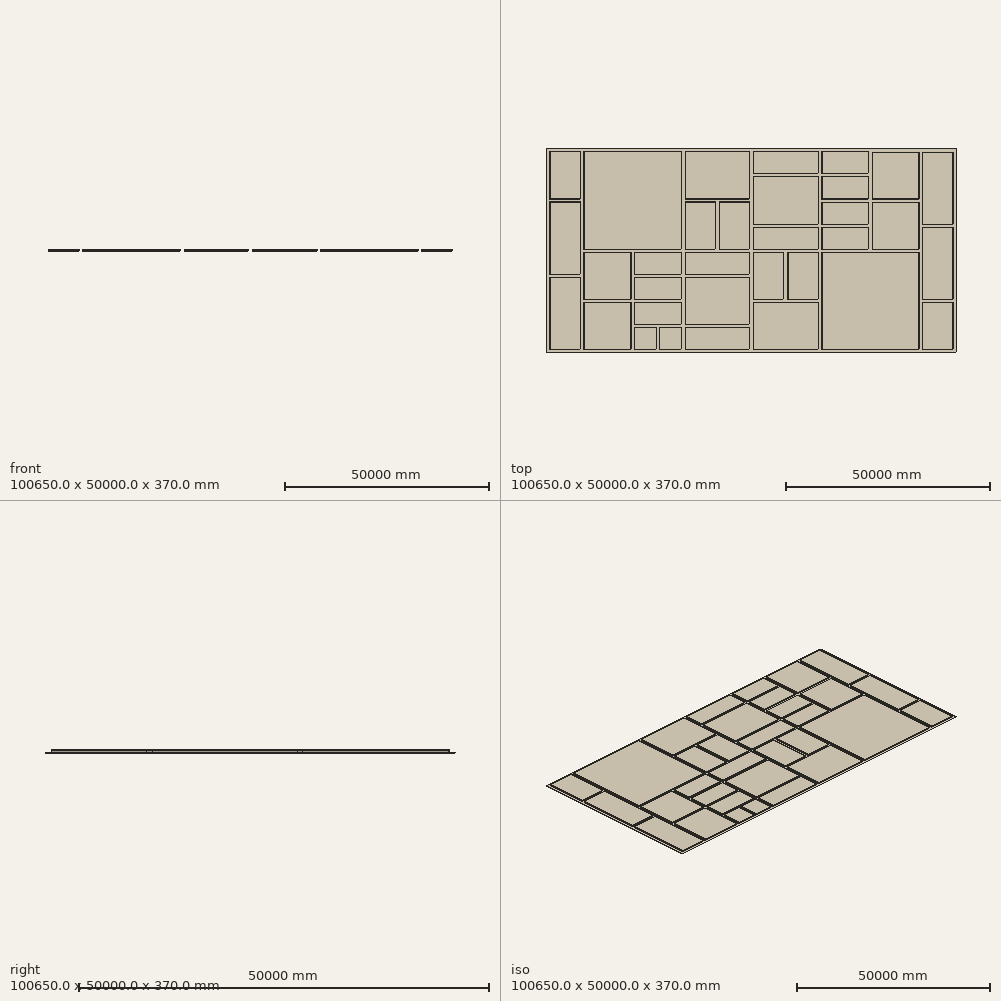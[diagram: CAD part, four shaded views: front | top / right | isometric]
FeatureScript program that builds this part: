
annotation { "Feature Type Name" : "Feature", "Feature Type Description" : "" }
export const myFeature = defineFeature(function(context is Context, id is Id, definition is map)
    precondition{}
    {
        {
            var Q0;
            Q0=qCreatedBy(makeId("Top.planeOp"),FACE);
            var sketch = newSketch(context, id + "F0", { "sketchPlane" : qUnion([Q0])});
            skLineSegment(sketch, "E0.bottom", {"start": v(50325, 25000) * mm, "end": v(-50325, 25000) * mm});
            skLineSegment(sketch, "E0.top", {"start": v(50325, -25000) * mm, "end": v(-50325, -25000) * mm});
            skLineSegment(sketch, "E0.left", {"start": v(50325, 25000) * mm, "end": v(50325, -25000) * mm});
            skLineSegment(sketch, "E0.right", {"start": v(-50325, 25000) * mm, "end": v(-50325, -25000) * mm});
            skPoint(sketch, "E0.middle", {"position": v(0, 0) * mm});
            skLineSegment(sketch, "E1", {"start": v(-50325, 0) * mm, "end": v(50325, 0) * mm, "construction": true});
            skLineSegment(sketch, "E2", {"start": v(-50688.62, 0) * mm, "end": v(50688.62, 0) * mm, "construction": true});
            skLineSegment(sketch, "E3.bottom", {"start": v(-16275, 11925) * mm, "end": v(-8775, 11925) * mm});
            skLineSegment(sketch, "E3.top", {"start": v(-16275, 283.33) * mm, "end": v(-8775, 283.33) * mm});
            skLineSegment(sketch, "E3.left", {"start": v(-16275, 11925) * mm, "end": v(-16275, 283.33) * mm});
            skLineSegment(sketch, "E3.right", {"start": v(-8775, 11925) * mm, "end": v(-8775, 283.33) * mm});
            skLineSegment(sketch, "E4.bottom", {"start": v(425, 18104.17) * mm, "end": v(16425, 18104.17) * mm});
            skLineSegment(sketch, "E4.top", {"start": v(425, 6391.67) * mm, "end": v(16425, 6391.67) * mm});
            skLineSegment(sketch, "E4.left", {"start": v(425, 18104.17) * mm, "end": v(425, 6391.67) * mm});
            skLineSegment(sketch, "E4.right", {"start": v(16425, 18104.17) * mm, "end": v(16425, 6391.67) * mm});
            skLineSegment(sketch, "E5.bottom", {"start": v(29625, 24141.67) * mm, "end": v(41125, 24141.67) * mm});
            skLineSegment(sketch, "E5.top", {"start": v(29625, 12641.67) * mm, "end": v(41125, 12641.67) * mm});
            skLineSegment(sketch, "E5.left", {"start": v(29625, 24141.67) * mm, "end": v(29625, 12641.67) * mm});
            skLineSegment(sketch, "E5.right", {"start": v(41125, 24141.67) * mm, "end": v(41125, 12641.67) * mm});
            skLineSegment(sketch, "E6.bottom", {"start": v(41975, 24141.67) * mm, "end": v(49475, 24141.67) * mm});
            skLineSegment(sketch, "E6.top", {"start": v(41975, 6391.67) * mm, "end": v(49475, 6391.67) * mm});
            skLineSegment(sketch, "E6.left", {"start": v(41975, 24141.67) * mm, "end": v(41975, 6391.67) * mm});
            skLineSegment(sketch, "E6.right", {"start": v(49475, 24141.67) * mm, "end": v(49475, 6391.67) * mm});
            skLineSegment(sketch, "E7.bottom", {"start": v(-49475, 24283.33) * mm, "end": v(-41975, 24283.33) * mm});
            skLineSegment(sketch, "E7.top", {"start": v(-49475, 12641.67) * mm, "end": v(-41975, 12641.67) * mm});
            skLineSegment(sketch, "E7.left", {"start": v(-49475, 24283.33) * mm, "end": v(-49475, 12641.67) * mm});
            skLineSegment(sketch, "E7.right", {"start": v(-41975, 24283.33) * mm, "end": v(-41975, 12641.67) * mm});
            skLineSegment(sketch, "E8.bottom", {"start": v(-49475, 11925) * mm, "end": v(-41975, 11925) * mm});
            skLineSegment(sketch, "E8.top", {"start": v(-49475, -5862.5) * mm, "end": v(-41975, -5862.5) * mm});
            skLineSegment(sketch, "E8.left", {"start": v(-49475, 11925) * mm, "end": v(-49475, -5862.5) * mm});
            skLineSegment(sketch, "E8.right", {"start": v(-41975, 11925) * mm, "end": v(-41975, -5862.5) * mm});
            skLineSegment(sketch, "E9.bottom", {"start": v(-49475, -6579.17) * mm, "end": v(-41975, -6579.17) * mm});
            skLineSegment(sketch, "E9.top", {"start": v(-49475, -24283.33) * mm, "end": v(-41975, -24283.33) * mm});
            skLineSegment(sketch, "E9.left", {"start": v(-49475, -6579.17) * mm, "end": v(-49475, -24283.33) * mm});
            skLineSegment(sketch, "E9.right", {"start": v(-41975, -6579.17) * mm, "end": v(-41975, -24283.33) * mm});
            skLineSegment(sketch, "E10.bottom", {"start": v(-41125, -433.33) * mm, "end": v(-29550, -433.33) * mm});
            skLineSegment(sketch, "E10.top", {"start": v(-41125, -12008.33) * mm, "end": v(-29550, -12008.33) * mm});
            skLineSegment(sketch, "E10.left", {"start": v(-41125, -433.33) * mm, "end": v(-41125, -12008.33) * mm});
            skLineSegment(sketch, "E10.right", {"start": v(-29550, -433.33) * mm, "end": v(-29550, -12008.33) * mm});
            skLineSegment(sketch, "E11.bottom", {"start": v(-28700, -12725) * mm, "end": v(-17125, -12725) * mm});
            skLineSegment(sketch, "E11.top", {"start": v(-28700, -18137.5) * mm, "end": v(-17125, -18137.5) * mm});
            skLineSegment(sketch, "E11.left", {"start": v(-28700, -12725) * mm, "end": v(-28700, -18137.5) * mm});
            skLineSegment(sketch, "E11.right", {"start": v(-17125, -12725) * mm, "end": v(-17125, -18137.5) * mm});
            skLineSegment(sketch, "E12.bottom", {"start": v(-28700, -433.33) * mm, "end": v(-17125, -433.33) * mm});
            skLineSegment(sketch, "E12.top", {"start": v(-28700, -5862.5) * mm, "end": v(-17125, -5862.5) * mm});
            skLineSegment(sketch, "E12.left", {"start": v(-28700, -433.33) * mm, "end": v(-28700, -5862.5) * mm});
            skLineSegment(sketch, "E12.right", {"start": v(-17125, -433.33) * mm, "end": v(-17125, -5862.5) * mm});
            skLineSegment(sketch, "E13.bottom", {"start": v(-28700, -6579.17) * mm, "end": v(-17125, -6579.17) * mm});
            skLineSegment(sketch, "E13.top", {"start": v(-28700, -12008.33) * mm, "end": v(-17125, -12008.33) * mm});
            skLineSegment(sketch, "E13.left", {"start": v(-28700, -6579.17) * mm, "end": v(-28700, -12008.33) * mm});
            skLineSegment(sketch, "E13.right", {"start": v(-17125, -6579.17) * mm, "end": v(-17125, -12008.33) * mm});
            skLineSegment(sketch, "E14.bottom", {"start": v(-41125, -12725) * mm, "end": v(-29550, -12725) * mm});
            skLineSegment(sketch, "E14.top", {"start": v(-41125, -24283.33) * mm, "end": v(-29550, -24283.33) * mm});
            skLineSegment(sketch, "E14.left", {"start": v(-41125, -12725) * mm, "end": v(-41125, -24283.33) * mm});
            skLineSegment(sketch, "E14.right", {"start": v(-29550, -12725) * mm, "end": v(-29550, -24283.33) * mm});
            skPoint(sketch, "E15.oppositeSnap0", {"position": v(-45725, -24283.33) * mm});
            skLineSegment(sketch, "E15.bottom", {"start": v(-28700, -18854.17) * mm, "end": v(-23270.83, -18854.17) * mm});
            skLineSegment(sketch, "E15.top", {"start": v(-28700, -24283.33) * mm, "end": v(-23270.83, -24283.33) * mm});
            skLineSegment(sketch, "E15.left", {"start": v(-28700, -18854.17) * mm, "end": v(-28700, -24283.33) * mm});
            skLineSegment(sketch, "E15.right", {"start": v(-23270.83, -18854.17) * mm, "end": v(-23270.83, -24283.33) * mm});
            skLineSegment(sketch, "E16.bottom", {"start": v(-22554.17, -18854.17) * mm, "end": v(-17125, -18854.17) * mm});
            skLineSegment(sketch, "E16.top", {"start": v(-22554.17, -24283.33) * mm, "end": v(-17125, -24283.33) * mm});
            skLineSegment(sketch, "E16.left", {"start": v(-22554.17, -18854.17) * mm, "end": v(-22554.17, -24283.33) * mm});
            skLineSegment(sketch, "E16.right", {"start": v(-17125, -18854.17) * mm, "end": v(-17125, -24283.33) * mm});
            skLineSegment(sketch, "E17.bottom", {"start": v(-41125, 24283.33) * mm, "end": v(-17125, 24283.33) * mm});
            skLineSegment(sketch, "E17.top", {"start": v(-41125, 283.33) * mm, "end": v(-17125, 283.33) * mm});
            skLineSegment(sketch, "E17.left", {"start": v(-41125, 24283.33) * mm, "end": v(-41125, 283.33) * mm});
            skLineSegment(sketch, "E17.right", {"start": v(-17125, 24283.33) * mm, "end": v(-17125, 283.33) * mm});
            skLineSegment(sketch, "E18.bottom", {"start": v(-7925, 11925) * mm, "end": v(-425, 11925) * mm});
            skLineSegment(sketch, "E18.top", {"start": v(-7925, 283.33) * mm, "end": v(-425, 283.33) * mm});
            skLineSegment(sketch, "E18.left", {"start": v(-7925, 11925) * mm, "end": v(-7925, 283.33) * mm});
            skLineSegment(sketch, "E18.right", {"start": v(-425, 11925) * mm, "end": v(-425, 283.33) * mm});
            skLineSegment(sketch, "E19.bottom", {"start": v(-16275, -433.33) * mm, "end": v(-425, -433.33) * mm});
            skLineSegment(sketch, "E19.top", {"start": v(-16275, -5862.5) * mm, "end": v(-425, -5862.5) * mm});
            skLineSegment(sketch, "E19.left", {"start": v(-16275, -433.33) * mm, "end": v(-16275, -5862.5) * mm});
            skLineSegment(sketch, "E19.right", {"start": v(-425, -433.33) * mm, "end": v(-425, -5862.5) * mm});
            skLineSegment(sketch, "E20.bottom", {"start": v(-16275, -6579.17) * mm, "end": v(-425, -6579.17) * mm});
            skLineSegment(sketch, "E20.top", {"start": v(-16275, -18137.5) * mm, "end": v(-425, -18137.5) * mm});
            skLineSegment(sketch, "E20.left", {"start": v(-16275, -6579.17) * mm, "end": v(-16275, -18137.5) * mm});
            skLineSegment(sketch, "E20.right", {"start": v(-425, -6579.17) * mm, "end": v(-425, -18137.5) * mm});
            skLineSegment(sketch, "E21.bottom", {"start": v(-16275, -24283.33) * mm, "end": v(-425, -24283.33) * mm});
            skLineSegment(sketch, "E21.top", {"start": v(-16275, -18854.17) * mm, "end": v(-425, -18854.17) * mm});
            skLineSegment(sketch, "E21.left", {"start": v(-16275, -24283.33) * mm, "end": v(-16275, -18854.17) * mm});
            skLineSegment(sketch, "E21.right", {"start": v(-425, -24283.33) * mm, "end": v(-425, -18854.17) * mm});
            skLineSegment(sketch, "E22.bottom", {"start": v(425, -12725) * mm, "end": v(16425, -12725) * mm});
            skLineSegment(sketch, "E22.top", {"start": v(425, -24283.33) * mm, "end": v(16425, -24283.33) * mm});
            skLineSegment(sketch, "E22.left", {"start": v(425, -12725) * mm, "end": v(425, -24283.33) * mm});
            skLineSegment(sketch, "E22.right", {"start": v(16425, -12725) * mm, "end": v(16425, -24283.33) * mm});
            skLineSegment(sketch, "E23.bottom", {"start": v(425, -433.33) * mm, "end": v(7925, -433.33) * mm});
            skLineSegment(sketch, "E23.top", {"start": v(425, -12008.33) * mm, "end": v(7925, -12008.33) * mm});
            skLineSegment(sketch, "E23.left", {"start": v(425, -433.33) * mm, "end": v(425, -12008.33) * mm});
            skLineSegment(sketch, "E23.right", {"start": v(7925, -433.33) * mm, "end": v(7925, -12008.33) * mm});
            skLineSegment(sketch, "E24.bottom", {"start": v(8925, -433.33) * mm, "end": v(16425, -433.33) * mm});
            skLineSegment(sketch, "E24.top", {"start": v(8925, -12008.33) * mm, "end": v(16425, -12008.33) * mm});
            skLineSegment(sketch, "E24.left", {"start": v(8925, -433.33) * mm, "end": v(8925, -12008.33) * mm});
            skLineSegment(sketch, "E24.right", {"start": v(16425, -433.33) * mm, "end": v(16425, -12008.33) * mm});
            skLineSegment(sketch, "E25.bottom", {"start": v(425, 24283.33) * mm, "end": v(16425, 24283.33) * mm});
            skLineSegment(sketch, "E25.top", {"start": v(425, 18820.83) * mm, "end": v(16425, 18820.83) * mm});
            skLineSegment(sketch, "E25.left", {"start": v(425, 24283.33) * mm, "end": v(425, 18820.83) * mm});
            skLineSegment(sketch, "E25.right", {"start": v(16425, 24283.33) * mm, "end": v(16425, 18820.83) * mm});
            skLineSegment(sketch, "E26.bottom", {"start": v(17275, 24283.33) * mm, "end": v(28775, 24283.33) * mm});
            skLineSegment(sketch, "E26.top", {"start": v(17275, 18820.83) * mm, "end": v(28775, 18820.83) * mm});
            skLineSegment(sketch, "E26.left", {"start": v(17275, 24283.33) * mm, "end": v(17275, 18820.83) * mm});
            skLineSegment(sketch, "E26.right", {"start": v(28775, 24283.33) * mm, "end": v(28775, 18820.83) * mm});
            skLineSegment(sketch, "E27.bottom", {"start": v(17275, 18104.17) * mm, "end": v(28775, 18104.17) * mm});
            skLineSegment(sketch, "E27.top", {"start": v(17275, 12641.67) * mm, "end": v(28775, 12641.67) * mm});
            skLineSegment(sketch, "E27.left", {"start": v(17275, 18104.17) * mm, "end": v(17275, 12641.67) * mm});
            skLineSegment(sketch, "E27.right", {"start": v(28775, 18104.17) * mm, "end": v(28775, 12641.67) * mm});
            skLineSegment(sketch, "E28.bottom", {"start": v(17275, 11783.33) * mm, "end": v(28775, 11783.33) * mm});
            skLineSegment(sketch, "E28.top", {"start": v(17275, 6391.67) * mm, "end": v(28775, 6391.67) * mm});
            skLineSegment(sketch, "E28.left", {"start": v(17275, 11783.33) * mm, "end": v(17275, 6391.67) * mm});
            skLineSegment(sketch, "E28.right", {"start": v(28775, 11783.33) * mm, "end": v(28775, 6391.67) * mm});
            skLineSegment(sketch, "E29.bottom", {"start": v(425, 5675) * mm, "end": v(16425, 5675) * mm});
            skLineSegment(sketch, "E29.top", {"start": v(425, 283.33) * mm, "end": v(16425, 283.33) * mm});
            skLineSegment(sketch, "E29.left", {"start": v(425, 5675) * mm, "end": v(425, 283.33) * mm});
            skLineSegment(sketch, "E29.right", {"start": v(16425, 5675) * mm, "end": v(16425, 283.33) * mm});
            skLineSegment(sketch, "E30.bottom", {"start": v(17275, 5675) * mm, "end": v(28775, 5675) * mm});
            skLineSegment(sketch, "E30.top", {"start": v(17275, 283.33) * mm, "end": v(28775, 283.33) * mm});
            skLineSegment(sketch, "E30.left", {"start": v(17275, 5675) * mm, "end": v(17275, 283.33) * mm});
            skLineSegment(sketch, "E30.right", {"start": v(28775, 5675) * mm, "end": v(28775, 283.33) * mm});
            skLineSegment(sketch, "E31.bottom", {"start": v(29625, 11783.33) * mm, "end": v(41125, 11783.33) * mm});
            skLineSegment(sketch, "E31.top", {"start": v(29625, 283.33) * mm, "end": v(41125, 283.33) * mm});
            skLineSegment(sketch, "E31.left", {"start": v(29625, 11783.33) * mm, "end": v(29625, 283.33) * mm});
            skLineSegment(sketch, "E31.right", {"start": v(41125, 11783.33) * mm, "end": v(41125, 283.33) * mm});
            skLineSegment(sketch, "E32.bottom", {"start": v(17275, -433.33) * mm, "end": v(41125, -433.33) * mm});
            skLineSegment(sketch, "E32.top", {"start": v(17275, -24283.33) * mm, "end": v(41125, -24283.33) * mm});
            skLineSegment(sketch, "E32.left", {"start": v(17275, -433.33) * mm, "end": v(17275, -24283.33) * mm});
            skLineSegment(sketch, "E32.right", {"start": v(41125, -433.33) * mm, "end": v(41125, -24283.33) * mm});
            skLineSegment(sketch, "E33.bottom", {"start": v(41975, 5675) * mm, "end": v(49475, 5675) * mm});
            skLineSegment(sketch, "E33.top", {"start": v(41975, -12008.33) * mm, "end": v(49475, -12008.33) * mm});
            skLineSegment(sketch, "E33.left", {"start": v(41975, 5675) * mm, "end": v(41975, -12008.33) * mm});
            skLineSegment(sketch, "E33.right", {"start": v(49475, 5675) * mm, "end": v(49475, -12008.33) * mm});
            skLineSegment(sketch, "E34.bottom", {"start": v(41975, -12725) * mm, "end": v(49475, -12725) * mm});
            skLineSegment(sketch, "E34.top", {"start": v(41975, -24283.33) * mm, "end": v(49475, -24283.33) * mm});
            skLineSegment(sketch, "E34.left", {"start": v(41975, -12725) * mm, "end": v(41975, -24283.33) * mm});
            skLineSegment(sketch, "E34.right", {"start": v(49475, -12725) * mm, "end": v(49475, -24283.33) * mm});
            skLineSegment(sketch, "E35.bottom", {"start": v(-16275, 24283.33) * mm, "end": v(-425, 24283.33) * mm});
            skLineSegment(sketch, "E35.top", {"start": v(-16275, 12641.67) * mm, "end": v(-425, 12641.67) * mm});
            skLineSegment(sketch, "E35.left", {"start": v(-16275, 24283.33) * mm, "end": v(-16275, 12641.67) * mm});
            skLineSegment(sketch, "E35.right", {"start": v(-425, 24283.33) * mm, "end": v(-425, 12641.67) * mm});
            skLineSegment(sketch, "E36", {"start": v(-41975, 11925) * mm, "end": v(-41125, 11925) * mm, "construction": true});
            skLineSegment(sketch, "E37", {"start": v(-16275, 11925) * mm, "end": v(-17125, 11925) * mm, "construction": true});
            skLineSegment(sketch, "E38", {"start": v(-8775, 11925) * mm, "end": v(-7925, 11925) * mm, "construction": true});
            skLineSegment(sketch, "E39", {"start": v(-425, 11925) * mm, "end": v(425, 11925) * mm, "construction": true});
            skLineSegment(sketch, "E40", {"start": v(17275, 11783.33) * mm, "end": v(16425, 11783.33) * mm, "construction": true});
            skLineSegment(sketch, "E41", {"start": v(29625, 11783.33) * mm, "end": v(28775, 11783.33) * mm, "construction": true});
            skLineSegment(sketch, "E42", {"start": v(41125, 11783.33) * mm, "end": v(41975, 11783.33) * mm, "construction": true});
            skLineSegment(sketch, "E43", {"start": v(-16275, 24283.33) * mm, "end": v(-16275, 25000) * mm, "construction": true});
            skLineSegment(sketch, "E44", {"start": v(-16275, 11925) * mm, "end": v(-16275, 12641.67) * mm, "construction": true});
            skLineSegment(sketch, "E45", {"start": v(-16275, 283.33) * mm, "end": v(-16275, -433.33) * mm, "construction": true});
            skLineSegment(sketch, "E46", {"start": v(-16275, -5862.5) * mm, "end": v(-16275, -6579.17) * mm, "construction": true});
            skLineSegment(sketch, "E47", {"start": v(-16275, -18137.5) * mm, "end": v(-16275, -18854.17) * mm, "construction": true});
            skLineSegment(sketch, "E48", {"start": v(-16275, -24283.33) * mm, "end": v(-16275, -25000) * mm, "construction": true});
            skLineSegment(sketch, "E49", {"start": v(41975, -12008.33) * mm, "end": v(41975, -12725) * mm, "construction": true});
            skLineSegment(sketch, "E50", {"start": v(425, 6391.67) * mm, "end": v(425, 5675) * mm, "construction": true});
            skLineSegment(sketch, "E51", {"start": v(425, 18820.83) * mm, "end": v(425, 18104.17) * mm, "construction": true});
            skLineSegment(sketch, "E52", {"start": v(-29550, -12008.33) * mm, "end": v(-28700, -12008.33) * mm, "construction": true});
            skSolve(sketch);
        }
        {
            var Q0;
            Q0=makeQuery(id+"F0.imprint","IMPRINT",FACE,{"disambiguationData":[TD([[makeQuery(id+"F0.imprint","IMPRINT",EDGE,{"derivedFrom":sQuery(id+"F0.wireOp",EDGE,"E0.bottom")}),1.0]])]});
            extrude(context, id + "F1", {"entities" : qUnion([Q0]), "depth" : 25 * mm});
        }
        {
            var Q0;
            Q0=makeQuery(id+"F0.imprint","IMPRINT",FACE,{"disambiguationData":[TD([[makeQuery(id+"F0.imprint","IMPRINT",EDGE,{"derivedFrom":sQuery(id+"F0.wireOp",EDGE,"E17.bottom")}),-1.0]])]});
            var Q1;
            Q1=makeQuery(id+"F0.imprint","IMPRINT",FACE,{"disambiguationData":[TD([[makeQuery(id+"F0.imprint","IMPRINT",EDGE,{"derivedFrom":sQuery(id+"F0.wireOp",EDGE,"E4.bottom")}),-1.0]])]});
            var Q2;
            Q2=makeQuery(id+"F0.imprint","IMPRINT",FACE,{"disambiguationData":[TD([[makeQuery(id+"F0.imprint","IMPRINT",EDGE,{"derivedFrom":sQuery(id+"F0.wireOp",EDGE,"E21.bottom")}),1.0]])]});
            extrude(context, id + "F2", {"entities" : qUnion([Q0, Q1, Q2]), "depth" : 350 * mm, "hasSecondDirection" : true, "secondDirectionOppositeDirection" : false, "secondDirectionDepth" : 280 * mm});
        }
        {
            var Q0;
            Q0=makeQuery(id+"F0.imprint","IMPRINT",FACE,{"disambiguationData":[TD([[makeQuery(id+"F0.imprint","IMPRINT",EDGE,{"derivedFrom":sQuery(id+"F0.wireOp",EDGE,"E25.bottom")}),-1.0]])]});
            var Q1;
            Q1=makeQuery(id+"F0.imprint","IMPRINT",FACE,{"disambiguationData":[TD([[makeQuery(id+"F0.imprint","IMPRINT",EDGE,{"derivedFrom":sQuery(id+"F0.wireOp",EDGE,"E20.bottom")}),-1.0]])]});
            var Q2;
            Q2=makeQuery(id+"F0.imprint","IMPRINT",FACE,{"disambiguationData":[TD([[makeQuery(id+"F0.imprint","IMPRINT",EDGE,{"derivedFrom":sQuery(id+"F0.wireOp",EDGE,"E32.bottom")}),-1.0]])]});
            extrude(context, id + "F3", {"entities" : qUnion([Q0, Q1, Q2]), "depth" : 350 * mm, "hasSecondDirection" : true, "secondDirectionOppositeDirection" : false, "secondDirectionDepth" : 280 * mm});
        }
        {
            var Q0;
            Q0=makeQuery(id+"F0.imprint","IMPRINT",FACE,{"disambiguationData":[TD([[makeQuery(id+"F0.imprint","IMPRINT",EDGE,{"derivedFrom":sQuery(id+"F0.wireOp",EDGE,"E35.bottom")}),-1.0]])]});
            var Q1;
            Q1=makeQuery(id+"F0.imprint","IMPRINT",FACE,{"disambiguationData":[TD([[makeQuery(id+"F0.imprint","IMPRINT",EDGE,{"derivedFrom":sQuery(id+"F0.wireOp",EDGE,"E26.bottom")}),-1.0]])]});
            var Q2;
            Q2=makeQuery(id+"F0.imprint","IMPRINT",FACE,{"disambiguationData":[TD([[makeQuery(id+"F0.imprint","IMPRINT",EDGE,{"derivedFrom":sQuery(id+"F0.wireOp",EDGE,"E6.bottom")}),-1.0]])]});
            var Q3;
            Q3=makeQuery(id+"F0.imprint","IMPRINT",FACE,{"disambiguationData":[TD([[makeQuery(id+"F0.imprint","IMPRINT",EDGE,{"derivedFrom":sQuery(id+"F0.wireOp",EDGE,"E22.bottom")}),-1.0]])]});
            var Q4;
            Q4=makeQuery(id+"F0.imprint","IMPRINT",FACE,{"disambiguationData":[TD([[makeQuery(id+"F0.imprint","IMPRINT",EDGE,{"derivedFrom":sQuery(id+"F0.wireOp",EDGE,"E15.bottom")}),-1.0]])]});
            var Q5;
            Q5=makeQuery(id+"F0.imprint","IMPRINT",FACE,{"disambiguationData":[TD([[makeQuery(id+"F0.imprint","IMPRINT",EDGE,{"derivedFrom":sQuery(id+"F0.wireOp",EDGE,"E9.bottom")}),-1.0]])]});
            extrude(context, id + "F4", {"entities" : qUnion([Q0, Q1, Q2, Q3, Q4, Q5]), "depth" : 350 * mm, "hasSecondDirection" : true, "secondDirectionOppositeDirection" : false, "secondDirectionDepth" : 280 * mm});
        }
        {
            var Q0;
            Q0=makeQuery(id+"F0.imprint","IMPRINT",FACE,{"disambiguationData":[TD([[makeQuery(id+"F0.imprint","IMPRINT",EDGE,{"derivedFrom":sQuery(id+"F0.wireOp",EDGE,"E27.bottom")}),-1.0]])]});
            var Q1;
            Q1=makeQuery(id+"F0.imprint","IMPRINT",FACE,{"disambiguationData":[TD([[makeQuery(id+"F0.imprint","IMPRINT",EDGE,{"derivedFrom":sQuery(id+"F0.wireOp",EDGE,"E31.bottom")}),-1.0]])]});
            var Q2;
            Q2=makeQuery(id+"F0.imprint","IMPRINT",FACE,{"disambiguationData":[TD([[makeQuery(id+"F0.imprint","IMPRINT",EDGE,{"derivedFrom":sQuery(id+"F0.wireOp",EDGE,"E11.bottom")}),-1.0]])]});
            var Q3;
            Q3=makeQuery(id+"F0.imprint","IMPRINT",FACE,{"disambiguationData":[TD([[makeQuery(id+"F0.imprint","IMPRINT",EDGE,{"derivedFrom":sQuery(id+"F0.wireOp",EDGE,"E10.bottom")}),-1.0]])]});
            extrude(context, id + "F5", {"entities" : qUnion([Q0, Q1, Q2, Q3]), "depth" : 350 * mm, "hasSecondDirection" : true, "secondDirectionOppositeDirection" : false, "secondDirectionDepth" : 280 * mm});
        }
        {
            var Q0;
            Q0=makeQuery(id+"F0.imprint","IMPRINT",FACE,{"disambiguationData":[TD([[makeQuery(id+"F0.imprint","IMPRINT",EDGE,{"derivedFrom":sQuery(id+"F0.wireOp",EDGE,"E7.bottom")}),-1.0]])]});
            var Q1;
            Q1=makeQuery(id+"F0.imprint","IMPRINT",FACE,{"disambiguationData":[TD([[makeQuery(id+"F0.imprint","IMPRINT",EDGE,{"derivedFrom":sQuery(id+"F0.wireOp",EDGE,"E8.bottom")}),-1.0]])]});
            var Q2;
            Q2=makeQuery(id+"F0.imprint","IMPRINT",FACE,{"disambiguationData":[TD([[makeQuery(id+"F0.imprint","IMPRINT",EDGE,{"derivedFrom":sQuery(id+"F0.wireOp",EDGE,"E14.bottom")}),-1.0]])]});
            var Q3;
            Q3=makeQuery(id+"F0.imprint","IMPRINT",FACE,{"disambiguationData":[TD([[makeQuery(id+"F0.imprint","IMPRINT",EDGE,{"derivedFrom":sQuery(id+"F0.wireOp",EDGE,"E16.bottom")}),-1.0]])]});
            var Q4;
            Q4=makeQuery(id+"F0.imprint","IMPRINT",FACE,{"disambiguationData":[TD([[makeQuery(id+"F0.imprint","IMPRINT",EDGE,{"derivedFrom":sQuery(id+"F0.wireOp",EDGE,"E13.bottom")}),-1.0]])]});
            var Q5;
            Q5=makeQuery(id+"F0.imprint","IMPRINT",FACE,{"disambiguationData":[TD([[makeQuery(id+"F0.imprint","IMPRINT",EDGE,{"derivedFrom":sQuery(id+"F0.wireOp",EDGE,"E12.bottom")}),-1.0]])]});
            var Q6;
            Q6=makeQuery(id+"F0.imprint","IMPRINT",FACE,{"disambiguationData":[TD([[makeQuery(id+"F0.imprint","IMPRINT",EDGE,{"derivedFrom":sQuery(id+"F0.wireOp",EDGE,"E19.bottom")}),-1.0]])]});
            var Q7;
            Q7=makeQuery(id+"F0.imprint","IMPRINT",FACE,{"disambiguationData":[TD([[makeQuery(id+"F0.imprint","IMPRINT",EDGE,{"derivedFrom":sQuery(id+"F0.wireOp",EDGE,"E3.bottom")}),-1.0]])]});
            var Q8;
            Q8=makeQuery(id+"F0.imprint","IMPRINT",FACE,{"disambiguationData":[TD([[makeQuery(id+"F0.imprint","IMPRINT",EDGE,{"derivedFrom":sQuery(id+"F0.wireOp",EDGE,"E18.bottom")}),-1.0]])]});
            var Q9;
            Q9=makeQuery(id+"F0.imprint","IMPRINT",FACE,{"disambiguationData":[TD([[makeQuery(id+"F0.imprint","IMPRINT",EDGE,{"derivedFrom":sQuery(id+"F0.wireOp",EDGE,"E5.bottom")}),-1.0]])]});
            var Q10;
            Q10=makeQuery(id+"F0.imprint","IMPRINT",FACE,{"disambiguationData":[TD([[makeQuery(id+"F0.imprint","IMPRINT",EDGE,{"derivedFrom":sQuery(id+"F0.wireOp",EDGE,"E28.bottom")}),-1.0]])]});
            var Q11;
            Q11=makeQuery(id+"F0.imprint","IMPRINT",FACE,{"disambiguationData":[TD([[makeQuery(id+"F0.imprint","IMPRINT",EDGE,{"derivedFrom":sQuery(id+"F0.wireOp",EDGE,"E30.bottom")}),-1.0]])]});
            var Q12;
            Q12=makeQuery(id+"F0.imprint","IMPRINT",FACE,{"disambiguationData":[TD([[makeQuery(id+"F0.imprint","IMPRINT",EDGE,{"derivedFrom":sQuery(id+"F0.wireOp",EDGE,"E29.bottom")}),-1.0]])]});
            var Q13;
            Q13=makeQuery(id+"F0.imprint","IMPRINT",FACE,{"disambiguationData":[TD([[makeQuery(id+"F0.imprint","IMPRINT",EDGE,{"derivedFrom":sQuery(id+"F0.wireOp",EDGE,"E24.bottom")}),-1.0]])]});
            var Q14;
            Q14=makeQuery(id+"F0.imprint","IMPRINT",FACE,{"disambiguationData":[TD([[makeQuery(id+"F0.imprint","IMPRINT",EDGE,{"derivedFrom":sQuery(id+"F0.wireOp",EDGE,"E23.bottom")}),-1.0]])]});
            var Q15;
            Q15=makeQuery(id+"F0.imprint","IMPRINT",FACE,{"disambiguationData":[TD([[makeQuery(id+"F0.imprint","IMPRINT",EDGE,{"derivedFrom":sQuery(id+"F0.wireOp",EDGE,"E33.bottom")}),-1.0]])]});
            var Q16;
            Q16=makeQuery(id+"F0.imprint","IMPRINT",FACE,{"disambiguationData":[TD([[makeQuery(id+"F0.imprint","IMPRINT",EDGE,{"derivedFrom":sQuery(id+"F0.wireOp",EDGE,"E34.bottom")}),-1.0]])]});
            extrude(context, id + "F6", {"entities" : qUnion([Q0, Q1, Q2, Q3, Q4, Q5, Q6, Q7, Q8, Q9, Q10, Q11, Q12, Q13, Q14, Q15, Q16]), "depth" : 350 * mm, "hasSecondDirection" : true, "secondDirectionOppositeDirection" : false, "secondDirectionDepth" : 280 * mm});
        }
        {
            var Q0;
            Q0=makeQuery(id+"F2.opExtrude","CAP_FACE",FACE,{"disambiguationData":[OSD([sQuery(id+"F0.wireOp",EDGE,"E17.bottom"),sQuery(id+"F0.wireOp",EDGE,"E17.top"),sQuery(id+"F0.wireOp",EDGE,"E17.left"),sQuery(id+"F0.wireOp",EDGE,"E17.right")])],"isStart":true});
            var Q1;
            Q1=makeQuery(id+"F2.opExtrude","CAP_FACE",FACE,{"disambiguationData":[OSD([sQuery(id+"F0.wireOp",EDGE,"E21.bottom"),sQuery(id+"F0.wireOp",EDGE,"E21.top"),sQuery(id+"F0.wireOp",EDGE,"E21.left"),sQuery(id+"F0.wireOp",EDGE,"E21.right")])],"isStart":true});
            var Q2;
            Q2=makeQuery(id+"F2.opExtrude","CAP_FACE",FACE,{"disambiguationData":[OSD([sQuery(id+"F0.wireOp",EDGE,"E4.bottom"),sQuery(id+"F0.wireOp",EDGE,"E4.top"),sQuery(id+"F0.wireOp",EDGE,"E4.left"),sQuery(id+"F0.wireOp",EDGE,"E4.right")])],"isStart":true});
            var Q3;
            Q3=makeQuery(id+"F4.opExtrude","CAP_FACE",FACE,{"disambiguationData":[OSD([sQuery(id+"F0.wireOp",EDGE,"E6.bottom"),sQuery(id+"F0.wireOp",EDGE,"E6.top"),sQuery(id+"F0.wireOp",EDGE,"E6.left"),sQuery(id+"F0.wireOp",EDGE,"E6.right")])],"isStart":true});
            var Q4;
            Q4=makeQuery(id+"F6.opExtrude","CAP_FACE",FACE,{"disambiguationData":[OSD([sQuery(id+"F0.wireOp",EDGE,"E33.bottom"),sQuery(id+"F0.wireOp",EDGE,"E33.top"),sQuery(id+"F0.wireOp",EDGE,"E33.left"),sQuery(id+"F0.wireOp",EDGE,"E33.right")])],"isStart":true});
            var Q5;
            Q5=makeQuery(id+"F6.opExtrude","CAP_FACE",FACE,{"disambiguationData":[OSD([sQuery(id+"F0.wireOp",EDGE,"E34.bottom"),sQuery(id+"F0.wireOp",EDGE,"E34.top"),sQuery(id+"F0.wireOp",EDGE,"E34.left"),sQuery(id+"F0.wireOp",EDGE,"E34.right")])],"isStart":true});
            var Q6;
            Q6=makeQuery(id+"F3.opExtrude","CAP_FACE",FACE,{"disambiguationData":[OSD([sQuery(id+"F0.wireOp",EDGE,"E32.bottom"),sQuery(id+"F0.wireOp",EDGE,"E32.top"),sQuery(id+"F0.wireOp",EDGE,"E32.left"),sQuery(id+"F0.wireOp",EDGE,"E32.right")])],"isStart":true});
            var Q7;
            Q7=makeQuery(id+"F5.opExtrude","CAP_FACE",FACE,{"disambiguationData":[OSD([sQuery(id+"F0.wireOp",EDGE,"E31.bottom"),sQuery(id+"F0.wireOp",EDGE,"E31.top"),sQuery(id+"F0.wireOp",EDGE,"E31.left"),sQuery(id+"F0.wireOp",EDGE,"E31.right")])],"isStart":true});
            var Q8;
            Q8=makeQuery(id+"F6.opExtrude","CAP_FACE",FACE,{"disambiguationData":[OSD([sQuery(id+"F0.wireOp",EDGE,"E5.bottom"),sQuery(id+"F0.wireOp",EDGE,"E5.top"),sQuery(id+"F0.wireOp",EDGE,"E5.left"),sQuery(id+"F0.wireOp",EDGE,"E5.right")])],"isStart":true});
            var Q9;
            Q9=makeQuery(id+"F4.opExtrude","CAP_FACE",FACE,{"disambiguationData":[OSD([sQuery(id+"F0.wireOp",EDGE,"E26.bottom"),sQuery(id+"F0.wireOp",EDGE,"E26.top"),sQuery(id+"F0.wireOp",EDGE,"E26.left"),sQuery(id+"F0.wireOp",EDGE,"E26.right")])],"isStart":true});
            var Q10;
            Q10=makeQuery(id+"F5.opExtrude","CAP_FACE",FACE,{"disambiguationData":[OSD([sQuery(id+"F0.wireOp",EDGE,"E27.bottom"),sQuery(id+"F0.wireOp",EDGE,"E27.top"),sQuery(id+"F0.wireOp",EDGE,"E27.left"),sQuery(id+"F0.wireOp",EDGE,"E27.right")])],"isStart":true});
            var Q11;
            Q11=makeQuery(id+"F6.opExtrude","CAP_FACE",FACE,{"disambiguationData":[OSD([sQuery(id+"F0.wireOp",EDGE,"E28.bottom"),sQuery(id+"F0.wireOp",EDGE,"E28.top"),sQuery(id+"F0.wireOp",EDGE,"E28.left"),sQuery(id+"F0.wireOp",EDGE,"E28.right")])],"isStart":true});
            var Q12;
            Q12=makeQuery(id+"F6.opExtrude","CAP_FACE",FACE,{"disambiguationData":[OSD([sQuery(id+"F0.wireOp",EDGE,"E30.bottom"),sQuery(id+"F0.wireOp",EDGE,"E30.top"),sQuery(id+"F0.wireOp",EDGE,"E30.left"),sQuery(id+"F0.wireOp",EDGE,"E30.right")])],"isStart":true});
            var Q13;
            Q13=makeQuery(id+"F6.opExtrude","CAP_FACE",FACE,{"disambiguationData":[OSD([sQuery(id+"F0.wireOp",EDGE,"E29.bottom"),sQuery(id+"F0.wireOp",EDGE,"E29.top"),sQuery(id+"F0.wireOp",EDGE,"E29.left"),sQuery(id+"F0.wireOp",EDGE,"E29.right")])],"isStart":true});
            var Q14;
            Q14=makeQuery(id+"F3.opExtrude","CAP_FACE",FACE,{"disambiguationData":[OSD([sQuery(id+"F0.wireOp",EDGE,"E25.bottom"),sQuery(id+"F0.wireOp",EDGE,"E25.top"),sQuery(id+"F0.wireOp",EDGE,"E25.left"),sQuery(id+"F0.wireOp",EDGE,"E25.right")])],"isStart":true});
            var Q15;
            Q15=makeQuery(id+"F6.opExtrude","CAP_FACE",FACE,{"disambiguationData":[OSD([sQuery(id+"F0.wireOp",EDGE,"E23.bottom"),sQuery(id+"F0.wireOp",EDGE,"E23.top"),sQuery(id+"F0.wireOp",EDGE,"E23.left"),sQuery(id+"F0.wireOp",EDGE,"E23.right")])],"isStart":true});
            var Q16;
            Q16=makeQuery(id+"F6.opExtrude","CAP_FACE",FACE,{"disambiguationData":[OSD([sQuery(id+"F0.wireOp",EDGE,"E24.bottom"),sQuery(id+"F0.wireOp",EDGE,"E24.top"),sQuery(id+"F0.wireOp",EDGE,"E24.left"),sQuery(id+"F0.wireOp",EDGE,"E24.right")])],"isStart":true});
            var Q17;
            Q17=makeQuery(id+"F4.opExtrude","CAP_FACE",FACE,{"disambiguationData":[OSD([sQuery(id+"F0.wireOp",EDGE,"E22.bottom"),sQuery(id+"F0.wireOp",EDGE,"E22.top"),sQuery(id+"F0.wireOp",EDGE,"E22.left"),sQuery(id+"F0.wireOp",EDGE,"E22.right")])],"isStart":true});
            var Q18;
            Q18=makeQuery(id+"F3.opExtrude","CAP_FACE",FACE,{"disambiguationData":[OSD([sQuery(id+"F0.wireOp",EDGE,"E20.bottom"),sQuery(id+"F0.wireOp",EDGE,"E20.top"),sQuery(id+"F0.wireOp",EDGE,"E20.left"),sQuery(id+"F0.wireOp",EDGE,"E20.right")])],"isStart":true});
            var Q19;
            Q19=makeQuery(id+"F6.opExtrude","CAP_FACE",FACE,{"disambiguationData":[OSD([sQuery(id+"F0.wireOp",EDGE,"E19.bottom"),sQuery(id+"F0.wireOp",EDGE,"E19.top"),sQuery(id+"F0.wireOp",EDGE,"E19.left"),sQuery(id+"F0.wireOp",EDGE,"E19.right")])],"isStart":true});
            var Q20;
            Q20=makeQuery(id+"F6.opExtrude","CAP_FACE",FACE,{"disambiguationData":[OSD([sQuery(id+"F0.wireOp",EDGE,"E3.bottom"),sQuery(id+"F0.wireOp",EDGE,"E3.top"),sQuery(id+"F0.wireOp",EDGE,"E3.left"),sQuery(id+"F0.wireOp",EDGE,"E3.right")])],"isStart":true});
            var Q21;
            Q21=makeQuery(id+"F6.opExtrude","CAP_FACE",FACE,{"disambiguationData":[OSD([sQuery(id+"F0.wireOp",EDGE,"E18.bottom"),sQuery(id+"F0.wireOp",EDGE,"E18.top"),sQuery(id+"F0.wireOp",EDGE,"E18.left"),sQuery(id+"F0.wireOp",EDGE,"E18.right")])],"isStart":true});
            var Q22;
            Q22=makeQuery(id+"F4.opExtrude","CAP_FACE",FACE,{"disambiguationData":[OSD([sQuery(id+"F0.wireOp",EDGE,"E35.bottom"),sQuery(id+"F0.wireOp",EDGE,"E35.top"),sQuery(id+"F0.wireOp",EDGE,"E35.left"),sQuery(id+"F0.wireOp",EDGE,"E35.right")])],"isStart":true});
            var Q23;
            Q23=makeQuery(id+"F6.opExtrude","CAP_FACE",FACE,{"disambiguationData":[OSD([sQuery(id+"F0.wireOp",EDGE,"E7.bottom"),sQuery(id+"F0.wireOp",EDGE,"E7.top"),sQuery(id+"F0.wireOp",EDGE,"E7.left"),sQuery(id+"F0.wireOp",EDGE,"E7.right")])],"isStart":true});
            var Q24;
            Q24=makeQuery(id+"F6.opExtrude","CAP_FACE",FACE,{"disambiguationData":[OSD([sQuery(id+"F0.wireOp",EDGE,"E8.bottom"),sQuery(id+"F0.wireOp",EDGE,"E8.top"),sQuery(id+"F0.wireOp",EDGE,"E8.left"),sQuery(id+"F0.wireOp",EDGE,"E8.right")])],"isStart":true});
            var Q25;
            Q25=makeQuery(id+"F4.opExtrude","CAP_FACE",FACE,{"disambiguationData":[OSD([sQuery(id+"F0.wireOp",EDGE,"E9.bottom"),sQuery(id+"F0.wireOp",EDGE,"E9.top"),sQuery(id+"F0.wireOp",EDGE,"E9.left"),sQuery(id+"F0.wireOp",EDGE,"E9.right")])],"isStart":true});
            var Q26;
            Q26=makeQuery(id+"F5.opExtrude","CAP_FACE",FACE,{"disambiguationData":[OSD([sQuery(id+"F0.wireOp",EDGE,"E10.bottom"),sQuery(id+"F0.wireOp",EDGE,"E10.top"),sQuery(id+"F0.wireOp",EDGE,"E10.left"),sQuery(id+"F0.wireOp",EDGE,"E10.right")])],"isStart":true});
            var Q27;
            Q27=makeQuery(id+"F6.opExtrude","CAP_FACE",FACE,{"disambiguationData":[OSD([sQuery(id+"F0.wireOp",EDGE,"E12.bottom"),sQuery(id+"F0.wireOp",EDGE,"E12.top"),sQuery(id+"F0.wireOp",EDGE,"E12.left"),sQuery(id+"F0.wireOp",EDGE,"E12.right")])],"isStart":true});
            var Q28;
            Q28=makeQuery(id+"F6.opExtrude","CAP_FACE",FACE,{"disambiguationData":[OSD([sQuery(id+"F0.wireOp",EDGE,"E13.bottom"),sQuery(id+"F0.wireOp",EDGE,"E13.top"),sQuery(id+"F0.wireOp",EDGE,"E13.left"),sQuery(id+"F0.wireOp",EDGE,"E13.right")])],"isStart":true});
            var Q29;
            Q29=makeQuery(id+"F5.opExtrude","CAP_FACE",FACE,{"disambiguationData":[OSD([sQuery(id+"F0.wireOp",EDGE,"E11.bottom"),sQuery(id+"F0.wireOp",EDGE,"E11.top"),sQuery(id+"F0.wireOp",EDGE,"E11.left"),sQuery(id+"F0.wireOp",EDGE,"E11.right")])],"isStart":true});
            var Q30;
            Q30=makeQuery(id+"F6.opExtrude","CAP_FACE",FACE,{"disambiguationData":[OSD([sQuery(id+"F0.wireOp",EDGE,"E16.bottom"),sQuery(id+"F0.wireOp",EDGE,"E16.top"),sQuery(id+"F0.wireOp",EDGE,"E16.left"),sQuery(id+"F0.wireOp",EDGE,"E16.right")])],"isStart":true});
            var Q31;
            Q31=makeQuery(id+"F4.opExtrude","CAP_FACE",FACE,{"disambiguationData":[OSD([sQuery(id+"F0.wireOp",EDGE,"E15.bottom"),sQuery(id+"F0.wireOp",EDGE,"E15.top"),sQuery(id+"F0.wireOp",EDGE,"E15.left"),sQuery(id+"F0.wireOp",EDGE,"E15.right")])],"isStart":true});
            var Q32;
            Q32=makeQuery(id+"F6.opExtrude","CAP_FACE",FACE,{"disambiguationData":[OSD([sQuery(id+"F0.wireOp",EDGE,"E14.bottom"),sQuery(id+"F0.wireOp",EDGE,"E14.top"),sQuery(id+"F0.wireOp",EDGE,"E14.left"),sQuery(id+"F0.wireOp",EDGE,"E14.right")])],"isStart":true});
            shell(context, id + "F7", {"entities" : qUnion([Q0, Q1, Q2, Q3, Q4, Q5, Q6, Q7, Q8, Q9, Q10, Q11, Q12, Q13, Q14, Q15, Q16, Q17, Q18, Q19, Q20, Q21, Q22, Q23, Q24, Q25, Q26, Q27, Q28, Q29, Q30, Q31, Q32]), "thickness" : 20 * mm, "oppositeDirection" : true});
        }
        {
            var Q0;
            Q0=makeQuery(id+"F0.imprint","IMPRINT",FACE,{"disambiguationData":[TD([[makeQuery(id+"F0.imprint","IMPRINT",EDGE,{"derivedFrom":sQuery(id+"F0.wireOp",EDGE,"E17.bottom")}),-1.0]])]});
            var Q1;
            Q1=makeQuery(id+"F0.imprint","IMPRINT",FACE,{"disambiguationData":[TD([[makeQuery(id+"F0.imprint","IMPRINT",EDGE,{"derivedFrom":sQuery(id+"F0.wireOp",EDGE,"E21.bottom")}),1.0]])]});
            var Q2;
            Q2=makeQuery(id+"F0.imprint","IMPRINT",FACE,{"disambiguationData":[TD([[makeQuery(id+"F0.imprint","IMPRINT",EDGE,{"derivedFrom":sQuery(id+"F0.wireOp",EDGE,"E4.bottom")}),-1.0]])]});
            var Q3;
            Q3=makeQuery(id+"F0.imprint","IMPRINT",FACE,{"disambiguationData":[TD([[makeQuery(id+"F0.imprint","IMPRINT",EDGE,{"derivedFrom":sQuery(id+"F0.wireOp",EDGE,"E22.bottom")}),-1.0]])]});
            var Q4;
            Q4=makeQuery(id+"F0.imprint","IMPRINT",FACE,{"disambiguationData":[TD([[makeQuery(id+"F0.imprint","IMPRINT",EDGE,{"derivedFrom":sQuery(id+"F0.wireOp",EDGE,"E20.bottom")}),-1.0]])]});
            var Q5;
            Q5=makeQuery(id+"F0.imprint","IMPRINT",FACE,{"disambiguationData":[TD([[makeQuery(id+"F0.imprint","IMPRINT",EDGE,{"derivedFrom":sQuery(id+"F0.wireOp",EDGE,"E16.bottom")}),-1.0]])]});
            var Q6;
            Q6=makeQuery(id+"F0.imprint","IMPRINT",FACE,{"disambiguationData":[TD([[makeQuery(id+"F0.imprint","IMPRINT",EDGE,{"derivedFrom":sQuery(id+"F0.wireOp",EDGE,"E15.bottom")}),-1.0]])]});
            var Q7;
            Q7=makeQuery(id+"F0.imprint","IMPRINT",FACE,{"disambiguationData":[TD([[makeQuery(id+"F0.imprint","IMPRINT",EDGE,{"derivedFrom":sQuery(id+"F0.wireOp",EDGE,"E11.bottom")}),-1.0]])]});
            var Q8;
            Q8=makeQuery(id+"F0.imprint","IMPRINT",FACE,{"disambiguationData":[TD([[makeQuery(id+"F0.imprint","IMPRINT",EDGE,{"derivedFrom":sQuery(id+"F0.wireOp",EDGE,"E14.bottom")}),-1.0]])]});
            var Q9;
            Q9=makeQuery(id+"F0.imprint","IMPRINT",FACE,{"disambiguationData":[TD([[makeQuery(id+"F0.imprint","IMPRINT",EDGE,{"derivedFrom":sQuery(id+"F0.wireOp",EDGE,"E9.bottom")}),-1.0]])]});
            var Q10;
            Q10=makeQuery(id+"F0.imprint","IMPRINT",FACE,{"disambiguationData":[TD([[makeQuery(id+"F0.imprint","IMPRINT",EDGE,{"derivedFrom":sQuery(id+"F0.wireOp",EDGE,"E8.bottom")}),-1.0]])]});
            var Q11;
            Q11=makeQuery(id+"F0.imprint","IMPRINT",FACE,{"disambiguationData":[TD([[makeQuery(id+"F0.imprint","IMPRINT",EDGE,{"derivedFrom":sQuery(id+"F0.wireOp",EDGE,"E10.bottom")}),-1.0]])]});
            var Q12;
            Q12=makeQuery(id+"F0.imprint","IMPRINT",FACE,{"disambiguationData":[TD([[makeQuery(id+"F0.imprint","IMPRINT",EDGE,{"derivedFrom":sQuery(id+"F0.wireOp",EDGE,"E12.bottom")}),-1.0]])]});
            var Q13;
            Q13=makeQuery(id+"F0.imprint","IMPRINT",FACE,{"disambiguationData":[TD([[makeQuery(id+"F0.imprint","IMPRINT",EDGE,{"derivedFrom":sQuery(id+"F0.wireOp",EDGE,"E13.bottom")}),-1.0]])]});
            var Q14;
            Q14=makeQuery(id+"F0.imprint","IMPRINT",FACE,{"disambiguationData":[TD([[makeQuery(id+"F0.imprint","IMPRINT",EDGE,{"derivedFrom":sQuery(id+"F0.wireOp",EDGE,"E19.bottom")}),-1.0]])]});
            var Q15;
            Q15=makeQuery(id+"F0.imprint","IMPRINT",FACE,{"disambiguationData":[TD([[makeQuery(id+"F0.imprint","IMPRINT",EDGE,{"derivedFrom":sQuery(id+"F0.wireOp",EDGE,"E23.bottom")}),-1.0]])]});
            var Q16;
            Q16=makeQuery(id+"F0.imprint","IMPRINT",FACE,{"disambiguationData":[TD([[makeQuery(id+"F0.imprint","IMPRINT",EDGE,{"derivedFrom":sQuery(id+"F0.wireOp",EDGE,"E24.bottom")}),-1.0]])]});
            var Q17;
            Q17=makeQuery(id+"F0.imprint","IMPRINT",FACE,{"disambiguationData":[TD([[makeQuery(id+"F0.imprint","IMPRINT",EDGE,{"derivedFrom":sQuery(id+"F0.wireOp",EDGE,"E32.bottom")}),-1.0]])]});
            var Q18;
            Q18=makeQuery(id+"F0.imprint","IMPRINT",FACE,{"disambiguationData":[TD([[makeQuery(id+"F0.imprint","IMPRINT",EDGE,{"derivedFrom":sQuery(id+"F0.wireOp",EDGE,"E31.bottom")}),-1.0]])]});
            var Q19;
            Q19=makeQuery(id+"F0.imprint","IMPRINT",FACE,{"disambiguationData":[TD([[makeQuery(id+"F0.imprint","IMPRINT",EDGE,{"derivedFrom":sQuery(id+"F0.wireOp",EDGE,"E28.bottom")}),-1.0]])]});
            var Q20;
            Q20=makeQuery(id+"F0.imprint","IMPRINT",FACE,{"disambiguationData":[TD([[makeQuery(id+"F0.imprint","IMPRINT",EDGE,{"derivedFrom":sQuery(id+"F0.wireOp",EDGE,"E30.bottom")}),-1.0]])]});
            var Q21;
            Q21=makeQuery(id+"F0.imprint","IMPRINT",FACE,{"disambiguationData":[TD([[makeQuery(id+"F0.imprint","IMPRINT",EDGE,{"derivedFrom":sQuery(id+"F0.wireOp",EDGE,"E29.bottom")}),-1.0]])]});
            var Q22;
            Q22=makeQuery(id+"F0.imprint","IMPRINT",FACE,{"disambiguationData":[TD([[makeQuery(id+"F0.imprint","IMPRINT",EDGE,{"derivedFrom":sQuery(id+"F0.wireOp",EDGE,"E18.bottom")}),-1.0]])]});
            var Q23;
            Q23=makeQuery(id+"F0.imprint","IMPRINT",FACE,{"disambiguationData":[TD([[makeQuery(id+"F0.imprint","IMPRINT",EDGE,{"derivedFrom":sQuery(id+"F0.wireOp",EDGE,"E3.bottom")}),-1.0]])]});
            var Q24;
            Q24=makeQuery(id+"F0.imprint","IMPRINT",FACE,{"disambiguationData":[TD([[makeQuery(id+"F0.imprint","IMPRINT",EDGE,{"derivedFrom":sQuery(id+"F0.wireOp",EDGE,"E35.bottom")}),-1.0]])]});
            var Q25;
            Q25=makeQuery(id+"F0.imprint","IMPRINT",FACE,{"disambiguationData":[TD([[makeQuery(id+"F0.imprint","IMPRINT",EDGE,{"derivedFrom":sQuery(id+"F0.wireOp",EDGE,"E25.bottom")}),-1.0]])]});
            var Q26;
            Q26=makeQuery(id+"F0.imprint","IMPRINT",FACE,{"disambiguationData":[TD([[makeQuery(id+"F0.imprint","IMPRINT",EDGE,{"derivedFrom":sQuery(id+"F0.wireOp",EDGE,"E26.bottom")}),-1.0]])]});
            var Q27;
            Q27=makeQuery(id+"F0.imprint","IMPRINT",FACE,{"disambiguationData":[TD([[makeQuery(id+"F0.imprint","IMPRINT",EDGE,{"derivedFrom":sQuery(id+"F0.wireOp",EDGE,"E5.bottom")}),-1.0]])]});
            var Q28;
            Q28=makeQuery(id+"F0.imprint","IMPRINT",FACE,{"disambiguationData":[TD([[makeQuery(id+"F0.imprint","IMPRINT",EDGE,{"derivedFrom":sQuery(id+"F0.wireOp",EDGE,"E7.bottom")}),-1.0]])]});
            var Q29;
            Q29=makeQuery(id+"F0.imprint","IMPRINT",FACE,{"disambiguationData":[TD([[makeQuery(id+"F0.imprint","IMPRINT",EDGE,{"derivedFrom":sQuery(id+"F0.wireOp",EDGE,"E27.bottom")}),-1.0]])]});
            var Q30;
            Q30=makeQuery(id+"F0.imprint","IMPRINT",FACE,{"disambiguationData":[TD([[makeQuery(id+"F0.imprint","IMPRINT",EDGE,{"derivedFrom":sQuery(id+"F0.wireOp",EDGE,"E34.bottom")}),-1.0]])]});
            var Q31;
            Q31=makeQuery(id+"F0.imprint","IMPRINT",FACE,{"disambiguationData":[TD([[makeQuery(id+"F0.imprint","IMPRINT",EDGE,{"derivedFrom":sQuery(id+"F0.wireOp",EDGE,"E6.bottom")}),-1.0]])]});
            var Q32;
            Q32=makeQuery(id+"F0.imprint","IMPRINT",FACE,{"disambiguationData":[TD([[makeQuery(id+"F0.imprint","IMPRINT",EDGE,{"derivedFrom":sQuery(id+"F0.wireOp",EDGE,"E33.bottom")}),-1.0]])]});
            extrude(context, id + "F8", {"entities" : qUnion([Q0, Q1, Q2, Q3, Q4, Q5, Q6, Q7, Q8, Q9, Q10, Q11, Q12, Q13, Q14, Q15, Q16, Q17, Q18, Q19, Q20, Q21, Q22, Q23, Q24, Q25, Q26, Q27, Q28, Q29, Q30, Q31, Q32]), "depth" : 280 * mm});
        }
        {
            var Q0;
            Q0=makeQuery(id+"F0.imprint","IMPRINT",FACE,{"disambiguationData":[TD([[makeQuery(id+"F0.imprint","IMPRINT",EDGE,{"derivedFrom":sQuery(id+"F0.wireOp",EDGE,"E6.bottom")}),-1.0]])]});
            var Q1;
            Q1=makeQuery(id+"F0.imprint","IMPRINT",FACE,{"disambiguationData":[TD([[makeQuery(id+"F0.imprint","IMPRINT",EDGE,{"derivedFrom":sQuery(id+"F0.wireOp",EDGE,"E33.bottom")}),-1.0]])]});
            var Q2;
            Q2=makeQuery(id+"F0.imprint","IMPRINT",FACE,{"disambiguationData":[TD([[makeQuery(id+"F0.imprint","IMPRINT",EDGE,{"derivedFrom":sQuery(id+"F0.wireOp",EDGE,"E34.bottom")}),-1.0]])]});
            var Q3;
            Q3=makeQuery(id+"F0.imprint","IMPRINT",FACE,{"disambiguationData":[TD([[makeQuery(id+"F0.imprint","IMPRINT",EDGE,{"derivedFrom":sQuery(id+"F0.wireOp",EDGE,"E32.bottom")}),-1.0]])]});
            var Q4;
            Q4=makeQuery(id+"F0.imprint","IMPRINT",FACE,{"disambiguationData":[TD([[makeQuery(id+"F0.imprint","IMPRINT",EDGE,{"derivedFrom":sQuery(id+"F0.wireOp",EDGE,"E31.bottom")}),-1.0]])]});
            var Q5;
            Q5=makeQuery(id+"F0.imprint","IMPRINT",FACE,{"disambiguationData":[TD([[makeQuery(id+"F0.imprint","IMPRINT",EDGE,{"derivedFrom":sQuery(id+"F0.wireOp",EDGE,"E5.bottom")}),-1.0]])]});
            var Q6;
            Q6=makeQuery(id+"F0.imprint","IMPRINT",FACE,{"disambiguationData":[TD([[makeQuery(id+"F0.imprint","IMPRINT",EDGE,{"derivedFrom":sQuery(id+"F0.wireOp",EDGE,"E26.bottom")}),-1.0]])]});
            var Q7;
            Q7=makeQuery(id+"F0.imprint","IMPRINT",FACE,{"disambiguationData":[TD([[makeQuery(id+"F0.imprint","IMPRINT",EDGE,{"derivedFrom":sQuery(id+"F0.wireOp",EDGE,"E27.bottom")}),-1.0]])]});
            var Q8;
            Q8=makeQuery(id+"F0.imprint","IMPRINT",FACE,{"disambiguationData":[TD([[makeQuery(id+"F0.imprint","IMPRINT",EDGE,{"derivedFrom":sQuery(id+"F0.wireOp",EDGE,"E28.bottom")}),-1.0]])]});
            var Q9;
            Q9=makeQuery(id+"F0.imprint","IMPRINT",FACE,{"disambiguationData":[TD([[makeQuery(id+"F0.imprint","IMPRINT",EDGE,{"derivedFrom":sQuery(id+"F0.wireOp",EDGE,"E30.bottom")}),-1.0]])]});
            var Q10;
            Q10=makeQuery(id+"F0.imprint","IMPRINT",FACE,{"disambiguationData":[TD([[makeQuery(id+"F0.imprint","IMPRINT",EDGE,{"derivedFrom":sQuery(id+"F0.wireOp",EDGE,"E22.bottom")}),-1.0]])]});
            var Q11;
            Q11=makeQuery(id+"F0.imprint","IMPRINT",FACE,{"disambiguationData":[TD([[makeQuery(id+"F0.imprint","IMPRINT",EDGE,{"derivedFrom":sQuery(id+"F0.wireOp",EDGE,"E23.bottom")}),-1.0]])]});
            var Q12;
            Q12=makeQuery(id+"F0.imprint","IMPRINT",FACE,{"disambiguationData":[TD([[makeQuery(id+"F0.imprint","IMPRINT",EDGE,{"derivedFrom":sQuery(id+"F0.wireOp",EDGE,"E24.bottom")}),-1.0]])]});
            var Q13;
            Q13=makeQuery(id+"F0.imprint","IMPRINT",FACE,{"disambiguationData":[TD([[makeQuery(id+"F0.imprint","IMPRINT",EDGE,{"derivedFrom":sQuery(id+"F0.wireOp",EDGE,"E29.bottom")}),-1.0]])]});
            var Q14;
            Q14=makeQuery(id+"F0.imprint","IMPRINT",FACE,{"disambiguationData":[TD([[makeQuery(id+"F0.imprint","IMPRINT",EDGE,{"derivedFrom":sQuery(id+"F0.wireOp",EDGE,"E4.bottom")}),-1.0]])]});
            var Q15;
            Q15=makeQuery(id+"F0.imprint","IMPRINT",FACE,{"disambiguationData":[TD([[makeQuery(id+"F0.imprint","IMPRINT",EDGE,{"derivedFrom":sQuery(id+"F0.wireOp",EDGE,"E25.bottom")}),-1.0]])]});
            var Q16;
            Q16=makeQuery(id+"F0.imprint","IMPRINT",FACE,{"disambiguationData":[TD([[makeQuery(id+"F0.imprint","IMPRINT",EDGE,{"derivedFrom":sQuery(id+"F0.wireOp",EDGE,"E35.bottom")}),-1.0]])]});
            var Q17;
            Q17=makeQuery(id+"F0.imprint","IMPRINT",FACE,{"disambiguationData":[TD([[makeQuery(id+"F0.imprint","IMPRINT",EDGE,{"derivedFrom":sQuery(id+"F0.wireOp",EDGE,"E3.bottom")}),-1.0]])]});
            var Q18;
            Q18=makeQuery(id+"F0.imprint","IMPRINT",FACE,{"disambiguationData":[TD([[makeQuery(id+"F0.imprint","IMPRINT",EDGE,{"derivedFrom":sQuery(id+"F0.wireOp",EDGE,"E18.bottom")}),-1.0]])]});
            var Q19;
            Q19=makeQuery(id+"F0.imprint","IMPRINT",FACE,{"disambiguationData":[TD([[makeQuery(id+"F0.imprint","IMPRINT",EDGE,{"derivedFrom":sQuery(id+"F0.wireOp",EDGE,"E19.bottom")}),-1.0]])]});
            var Q20;
            Q20=makeQuery(id+"F0.imprint","IMPRINT",FACE,{"disambiguationData":[TD([[makeQuery(id+"F0.imprint","IMPRINT",EDGE,{"derivedFrom":sQuery(id+"F0.wireOp",EDGE,"E20.bottom")}),-1.0]])]});
            var Q21;
            Q21=makeQuery(id+"F0.imprint","IMPRINT",FACE,{"disambiguationData":[TD([[makeQuery(id+"F0.imprint","IMPRINT",EDGE,{"derivedFrom":sQuery(id+"F0.wireOp",EDGE,"E21.bottom")}),1.0]])]});
            var Q22;
            Q22=makeQuery(id+"F0.imprint","IMPRINT",FACE,{"disambiguationData":[TD([[makeQuery(id+"F0.imprint","IMPRINT",EDGE,{"derivedFrom":sQuery(id+"F0.wireOp",EDGE,"E15.bottom")}),-1.0]])]});
            var Q23;
            Q23=makeQuery(id+"F0.imprint","IMPRINT",FACE,{"disambiguationData":[TD([[makeQuery(id+"F0.imprint","IMPRINT",EDGE,{"derivedFrom":sQuery(id+"F0.wireOp",EDGE,"E16.bottom")}),-1.0]])]});
            var Q24;
            Q24=makeQuery(id+"F0.imprint","IMPRINT",FACE,{"disambiguationData":[TD([[makeQuery(id+"F0.imprint","IMPRINT",EDGE,{"derivedFrom":sQuery(id+"F0.wireOp",EDGE,"E11.bottom")}),-1.0]])]});
            var Q25;
            Q25=makeQuery(id+"F0.imprint","IMPRINT",FACE,{"disambiguationData":[TD([[makeQuery(id+"F0.imprint","IMPRINT",EDGE,{"derivedFrom":sQuery(id+"F0.wireOp",EDGE,"E13.bottom")}),-1.0]])]});
            var Q26;
            Q26=makeQuery(id+"F0.imprint","IMPRINT",FACE,{"disambiguationData":[TD([[makeQuery(id+"F0.imprint","IMPRINT",EDGE,{"derivedFrom":sQuery(id+"F0.wireOp",EDGE,"E12.bottom")}),-1.0]])]});
            var Q27;
            Q27=makeQuery(id+"F0.imprint","IMPRINT",FACE,{"disambiguationData":[TD([[makeQuery(id+"F0.imprint","IMPRINT",EDGE,{"derivedFrom":sQuery(id+"F0.wireOp",EDGE,"E17.bottom")}),-1.0]])]});
            var Q28;
            Q28=makeQuery(id+"F0.imprint","IMPRINT",FACE,{"disambiguationData":[TD([[makeQuery(id+"F0.imprint","IMPRINT",EDGE,{"derivedFrom":sQuery(id+"F0.wireOp",EDGE,"E14.bottom")}),-1.0]])]});
            var Q29;
            Q29=makeQuery(id+"F0.imprint","IMPRINT",FACE,{"disambiguationData":[TD([[makeQuery(id+"F0.imprint","IMPRINT",EDGE,{"derivedFrom":sQuery(id+"F0.wireOp",EDGE,"E10.bottom")}),-1.0]])]});
            var Q30;
            Q30=makeQuery(id+"F0.imprint","IMPRINT",FACE,{"disambiguationData":[TD([[makeQuery(id+"F0.imprint","IMPRINT",EDGE,{"derivedFrom":sQuery(id+"F0.wireOp",EDGE,"E9.bottom")}),-1.0]])]});
            var Q31;
            Q31=makeQuery(id+"F0.imprint","IMPRINT",FACE,{"disambiguationData":[TD([[makeQuery(id+"F0.imprint","IMPRINT",EDGE,{"derivedFrom":sQuery(id+"F0.wireOp",EDGE,"E8.bottom")}),-1.0]])]});
            var Q32;
            Q32=makeQuery(id+"F0.imprint","IMPRINT",FACE,{"disambiguationData":[TD([[makeQuery(id+"F0.imprint","IMPRINT",EDGE,{"derivedFrom":sQuery(id+"F0.wireOp",EDGE,"E7.bottom")}),-1.0]])]});
            var Q33;
            Q33=makeQuery(id+"F0.imprint","IMPRINT",FACE,{"disambiguationData":[TD([[makeQuery(id+"F0.imprint","IMPRINT",EDGE,{"derivedFrom":sQuery(id+"F0.wireOp",EDGE,"E0.bottom")}),1.0]])]});
            extrude(context, id + "F9", {"entities" : qUnion([Q0, Q1, Q2, Q3, Q4, Q5, Q6, Q7, Q8, Q9, Q10, Q11, Q12, Q13, Q14, Q15, Q16, Q17, Q18, Q19, Q20, Q21, Q22, Q23, Q24, Q25, Q26, Q27, Q28, Q29, Q30, Q31, Q32, Q33]), "operationType" : NewBodyOperationType.ADD, "depth" : 20 * mm, "hasSecondDirection" : true, "secondDirectionOppositeDirection" : false, "secondDirectionDepth" : 10 * mm});
        }
        {
            var Q0;
            Q0=makeQuery(id+"F2.opExtrude","CAP_FACE",FACE,{"disambiguationData":[OSD([sQuery(id+"F0.wireOp",EDGE,"E17.bottom"),sQuery(id+"F0.wireOp",EDGE,"E17.top"),sQuery(id+"F0.wireOp",EDGE,"E17.left"),sQuery(id+"F0.wireOp",EDGE,"E17.right")])],"isStart":false});
            var Q1;
            Q1=makeQuery(id+"F6.opExtrude","CAP_FACE",FACE,{"disambiguationData":[OSD([sQuery(id+"F0.wireOp",EDGE,"E7.bottom"),sQuery(id+"F0.wireOp",EDGE,"E7.top"),sQuery(id+"F0.wireOp",EDGE,"E7.left"),sQuery(id+"F0.wireOp",EDGE,"E7.right")])],"isStart":false});
            var Q2;
            Q2=makeQuery(id+"F6.opExtrude","CAP_FACE",FACE,{"disambiguationData":[OSD([sQuery(id+"F0.wireOp",EDGE,"E8.bottom"),sQuery(id+"F0.wireOp",EDGE,"E8.top"),sQuery(id+"F0.wireOp",EDGE,"E8.left"),sQuery(id+"F0.wireOp",EDGE,"E8.right")])],"isStart":false});
            var Q3;
            Q3=makeQuery(id+"F4.opExtrude","CAP_FACE",FACE,{"disambiguationData":[OSD([sQuery(id+"F0.wireOp",EDGE,"E9.bottom"),sQuery(id+"F0.wireOp",EDGE,"E9.top"),sQuery(id+"F0.wireOp",EDGE,"E9.left"),sQuery(id+"F0.wireOp",EDGE,"E9.right")])],"isStart":false});
            var Q4;
            Q4=makeQuery(id+"F6.opExtrude","CAP_FACE",FACE,{"disambiguationData":[OSD([sQuery(id+"F0.wireOp",EDGE,"E14.bottom"),sQuery(id+"F0.wireOp",EDGE,"E14.top"),sQuery(id+"F0.wireOp",EDGE,"E14.left"),sQuery(id+"F0.wireOp",EDGE,"E14.right")])],"isStart":false});
            var Q5;
            Q5=makeQuery(id+"F5.opExtrude","CAP_FACE",FACE,{"disambiguationData":[OSD([sQuery(id+"F0.wireOp",EDGE,"E10.bottom"),sQuery(id+"F0.wireOp",EDGE,"E10.top"),sQuery(id+"F0.wireOp",EDGE,"E10.left"),sQuery(id+"F0.wireOp",EDGE,"E10.right")])],"isStart":false});
            var Q6;
            Q6=makeQuery(id+"F5.opExtrude","CAP_FACE",FACE,{"disambiguationData":[OSD([sQuery(id+"F0.wireOp",EDGE,"E11.bottom"),sQuery(id+"F0.wireOp",EDGE,"E11.top"),sQuery(id+"F0.wireOp",EDGE,"E11.left"),sQuery(id+"F0.wireOp",EDGE,"E11.right")])],"isStart":false});
            var Q7;
            Q7=makeQuery(id+"F4.opExtrude","CAP_FACE",FACE,{"disambiguationData":[OSD([sQuery(id+"F0.wireOp",EDGE,"E15.bottom"),sQuery(id+"F0.wireOp",EDGE,"E15.top"),sQuery(id+"F0.wireOp",EDGE,"E15.left"),sQuery(id+"F0.wireOp",EDGE,"E15.right")])],"isStart":false});
            var Q8;
            Q8=makeQuery(id+"F6.opExtrude","CAP_FACE",FACE,{"disambiguationData":[OSD([sQuery(id+"F0.wireOp",EDGE,"E16.bottom"),sQuery(id+"F0.wireOp",EDGE,"E16.top"),sQuery(id+"F0.wireOp",EDGE,"E16.left"),sQuery(id+"F0.wireOp",EDGE,"E16.right")])],"isStart":false});
            var Q9;
            Q9=makeQuery(id+"F6.opExtrude","CAP_FACE",FACE,{"disambiguationData":[OSD([sQuery(id+"F0.wireOp",EDGE,"E13.bottom"),sQuery(id+"F0.wireOp",EDGE,"E13.top"),sQuery(id+"F0.wireOp",EDGE,"E13.left"),sQuery(id+"F0.wireOp",EDGE,"E13.right")])],"isStart":false});
            var Q10;
            Q10=makeQuery(id+"F6.opExtrude","CAP_FACE",FACE,{"disambiguationData":[OSD([sQuery(id+"F0.wireOp",EDGE,"E12.bottom"),sQuery(id+"F0.wireOp",EDGE,"E12.top"),sQuery(id+"F0.wireOp",EDGE,"E12.left"),sQuery(id+"F0.wireOp",EDGE,"E12.right")])],"isStart":false});
            var Q11;
            Q11=makeQuery(id+"F2.opExtrude","CAP_FACE",FACE,{"disambiguationData":[OSD([sQuery(id+"F0.wireOp",EDGE,"E21.bottom"),sQuery(id+"F0.wireOp",EDGE,"E21.top"),sQuery(id+"F0.wireOp",EDGE,"E21.left"),sQuery(id+"F0.wireOp",EDGE,"E21.right")])],"isStart":false});
            var Q12;
            Q12=makeQuery(id+"F3.opExtrude","CAP_FACE",FACE,{"disambiguationData":[OSD([sQuery(id+"F0.wireOp",EDGE,"E20.bottom"),sQuery(id+"F0.wireOp",EDGE,"E20.top"),sQuery(id+"F0.wireOp",EDGE,"E20.left"),sQuery(id+"F0.wireOp",EDGE,"E20.right")])],"isStart":false});
            var Q13;
            Q13=makeQuery(id+"F6.opExtrude","CAP_FACE",FACE,{"disambiguationData":[OSD([sQuery(id+"F0.wireOp",EDGE,"E19.bottom"),sQuery(id+"F0.wireOp",EDGE,"E19.top"),sQuery(id+"F0.wireOp",EDGE,"E19.left"),sQuery(id+"F0.wireOp",EDGE,"E19.right")])],"isStart":false});
            var Q14;
            Q14=makeQuery(id+"F6.opExtrude","CAP_FACE",FACE,{"disambiguationData":[OSD([sQuery(id+"F0.wireOp",EDGE,"E18.bottom"),sQuery(id+"F0.wireOp",EDGE,"E18.top"),sQuery(id+"F0.wireOp",EDGE,"E18.left"),sQuery(id+"F0.wireOp",EDGE,"E18.right")])],"isStart":false});
            var Q15;
            Q15=makeQuery(id+"F6.opExtrude","CAP_FACE",FACE,{"disambiguationData":[OSD([sQuery(id+"F0.wireOp",EDGE,"E3.bottom"),sQuery(id+"F0.wireOp",EDGE,"E3.top"),sQuery(id+"F0.wireOp",EDGE,"E3.left"),sQuery(id+"F0.wireOp",EDGE,"E3.right")])],"isStart":false});
            var Q16;
            Q16=makeQuery(id+"F4.opExtrude","CAP_FACE",FACE,{"disambiguationData":[OSD([sQuery(id+"F0.wireOp",EDGE,"E35.bottom"),sQuery(id+"F0.wireOp",EDGE,"E35.top"),sQuery(id+"F0.wireOp",EDGE,"E35.left"),sQuery(id+"F0.wireOp",EDGE,"E35.right")])],"isStart":false});
            var Q17;
            Q17=makeQuery(id+"F2.opExtrude","CAP_FACE",FACE,{"disambiguationData":[OSD([sQuery(id+"F0.wireOp",EDGE,"E4.bottom"),sQuery(id+"F0.wireOp",EDGE,"E4.top"),sQuery(id+"F0.wireOp",EDGE,"E4.left"),sQuery(id+"F0.wireOp",EDGE,"E4.right")])],"isStart":false});
            var Q18;
            Q18=makeQuery(id+"F6.opExtrude","CAP_FACE",FACE,{"disambiguationData":[OSD([sQuery(id+"F0.wireOp",EDGE,"E29.bottom"),sQuery(id+"F0.wireOp",EDGE,"E29.top"),sQuery(id+"F0.wireOp",EDGE,"E29.left"),sQuery(id+"F0.wireOp",EDGE,"E29.right")])],"isStart":false});
            var Q19;
            Q19=makeQuery(id+"F6.opExtrude","CAP_FACE",FACE,{"disambiguationData":[OSD([sQuery(id+"F0.wireOp",EDGE,"E23.bottom"),sQuery(id+"F0.wireOp",EDGE,"E23.top"),sQuery(id+"F0.wireOp",EDGE,"E23.left"),sQuery(id+"F0.wireOp",EDGE,"E23.right")])],"isStart":false});
            var Q20;
            Q20=makeQuery(id+"F6.opExtrude","CAP_FACE",FACE,{"disambiguationData":[OSD([sQuery(id+"F0.wireOp",EDGE,"E24.bottom"),sQuery(id+"F0.wireOp",EDGE,"E24.top"),sQuery(id+"F0.wireOp",EDGE,"E24.left"),sQuery(id+"F0.wireOp",EDGE,"E24.right")])],"isStart":false});
            var Q21;
            Q21=makeQuery(id+"F4.opExtrude","CAP_FACE",FACE,{"disambiguationData":[OSD([sQuery(id+"F0.wireOp",EDGE,"E22.bottom"),sQuery(id+"F0.wireOp",EDGE,"E22.top"),sQuery(id+"F0.wireOp",EDGE,"E22.left"),sQuery(id+"F0.wireOp",EDGE,"E22.right")])],"isStart":false});
            var Q22;
            Q22=makeQuery(id+"F3.opExtrude","CAP_EDGE",EDGE,{"disambiguationData":[OSD([sQuery(id+"F0.wireOp",EDGE,"E25.right")])],"isStart":false});
            var Q23;
            Q23=makeQuery(id+"F3.opExtrude","CAP_FACE",FACE,{"disambiguationData":[OSD([sQuery(id+"F0.wireOp",EDGE,"E25.bottom"),sQuery(id+"F0.wireOp",EDGE,"E25.top"),sQuery(id+"F0.wireOp",EDGE,"E25.left"),sQuery(id+"F0.wireOp",EDGE,"E25.right")])],"isStart":false});
            var Q24;
            Q24=makeQuery(id+"F4.opExtrude","CAP_FACE",FACE,{"disambiguationData":[OSD([sQuery(id+"F0.wireOp",EDGE,"E26.bottom"),sQuery(id+"F0.wireOp",EDGE,"E26.top"),sQuery(id+"F0.wireOp",EDGE,"E26.left"),sQuery(id+"F0.wireOp",EDGE,"E26.right")])],"isStart":false});
            var Q25;
            Q25=makeQuery(id+"F5.opExtrude","CAP_FACE",FACE,{"disambiguationData":[OSD([sQuery(id+"F0.wireOp",EDGE,"E27.bottom"),sQuery(id+"F0.wireOp",EDGE,"E27.top"),sQuery(id+"F0.wireOp",EDGE,"E27.left"),sQuery(id+"F0.wireOp",EDGE,"E27.right")])],"isStart":false});
            var Q26;
            Q26=makeQuery(id+"F6.opExtrude","CAP_FACE",FACE,{"disambiguationData":[OSD([sQuery(id+"F0.wireOp",EDGE,"E28.bottom"),sQuery(id+"F0.wireOp",EDGE,"E28.top"),sQuery(id+"F0.wireOp",EDGE,"E28.left"),sQuery(id+"F0.wireOp",EDGE,"E28.right")])],"isStart":false});
            var Q27;
            Q27=makeQuery(id+"F6.opExtrude","CAP_FACE",FACE,{"disambiguationData":[OSD([sQuery(id+"F0.wireOp",EDGE,"E30.bottom"),sQuery(id+"F0.wireOp",EDGE,"E30.top"),sQuery(id+"F0.wireOp",EDGE,"E30.left"),sQuery(id+"F0.wireOp",EDGE,"E30.right")])],"isStart":false});
            var Q28;
            Q28=makeQuery(id+"F5.opExtrude","CAP_FACE",FACE,{"disambiguationData":[OSD([sQuery(id+"F0.wireOp",EDGE,"E31.bottom"),sQuery(id+"F0.wireOp",EDGE,"E31.top"),sQuery(id+"F0.wireOp",EDGE,"E31.left"),sQuery(id+"F0.wireOp",EDGE,"E31.right")])],"isStart":false});
            var Q29;
            Q29=makeQuery(id+"F6.opExtrude","CAP_FACE",FACE,{"disambiguationData":[OSD([sQuery(id+"F0.wireOp",EDGE,"E5.bottom"),sQuery(id+"F0.wireOp",EDGE,"E5.top"),sQuery(id+"F0.wireOp",EDGE,"E5.left"),sQuery(id+"F0.wireOp",EDGE,"E5.right")])],"isStart":false});
            var Q30;
            Q30=makeQuery(id+"F4.opExtrude","CAP_FACE",FACE,{"disambiguationData":[OSD([sQuery(id+"F0.wireOp",EDGE,"E6.bottom"),sQuery(id+"F0.wireOp",EDGE,"E6.top"),sQuery(id+"F0.wireOp",EDGE,"E6.left"),sQuery(id+"F0.wireOp",EDGE,"E6.right")])],"isStart":false});
            var Q31;
            Q31=makeQuery(id+"F6.opExtrude","CAP_FACE",FACE,{"disambiguationData":[OSD([sQuery(id+"F0.wireOp",EDGE,"E33.bottom"),sQuery(id+"F0.wireOp",EDGE,"E33.top"),sQuery(id+"F0.wireOp",EDGE,"E33.left"),sQuery(id+"F0.wireOp",EDGE,"E33.right")])],"isStart":false});
            var Q32;
            Q32=makeQuery(id+"F6.opExtrude","CAP_FACE",FACE,{"disambiguationData":[OSD([sQuery(id+"F0.wireOp",EDGE,"E34.bottom"),sQuery(id+"F0.wireOp",EDGE,"E34.top"),sQuery(id+"F0.wireOp",EDGE,"E34.left"),sQuery(id+"F0.wireOp",EDGE,"E34.right")])],"isStart":false});
            var Q33;
            Q33=makeQuery(id+"F3.opExtrude","CAP_FACE",FACE,{"disambiguationData":[OSD([sQuery(id+"F0.wireOp",EDGE,"E32.bottom"),sQuery(id+"F0.wireOp",EDGE,"E32.top"),sQuery(id+"F0.wireOp",EDGE,"E32.left"),sQuery(id+"F0.wireOp",EDGE,"E32.right")])],"isStart":false});
            fillet(context, id + "F10", {"entities" : qUnion([Q0, Q1, Q2, Q3, Q4, Q5, Q6, Q7, Q8, Q9, Q10, Q11, Q12, Q13, Q14, Q15, Q16, Q17, Q18, Q19, Q20, Q21, Q22, Q23, Q24, Q25, Q26, Q27, Q28, Q29, Q30, Q31, Q32, Q33]), "radius" : 60 * mm, "allowEdgeOverflow" : false});
        }
    });
